# Revit family: 47388 - Ifö Sense High Cabinet with doors, white
name_source: partatom
category: Generic Models
revit_build: Autodesk Revit 2015 (Build: 20140606_1530(x64)
units: mm (PartAtom-declared; Revit-internal decimal feet)

## types (1)
- 47388 - Ifö Sense High Cabinet with doors, white
    BIMObjectName = 47388 - Ifö Sense High Cabinet with doors, white
    Brand = Ifö
    CabinetMaterial = MDF Chipboard
    Category = WashHandBasin
    Color = White
    Depth = 210 mm  [stored 0.688976 ft]
    Description = Ifö Sense half high cabinet with door
    DrainSize = 0 mm  [stored 0 ft]
    Features = feature1, feature2, feature59
    Handle = Metal-Steel
    Height = 1105 mm  [stored 3.62533 ft]
    Manufacturer = Geberit
    Material = MDF Chipboard
    Model = Ifö Sense High Cabinet with doors, white
    ModelNumber = 47388
    ModelReference = Sense
    MountingHeight(offset) = 1365 mm  [stored 4.47835 ft]
    Name = Ifö Sense half high cabinet with door
    NominalDepth = 210 mm  [stored 0.688976 ft]
    NominalHeight = 1105 mm  [stored 3.62533 ft]
    NominalWidth = 320 mm  [stored 1.04987 ft]
    Panel = White
    Serie = Sense
    Shape = Square
    Size = 320x1105x210
    Type = Building element
    URL.dk = http://www.ifo.dk
    URL.no = http://www.ifosanitar.no
    URL.se = http://www.ifo.se
    Width = 320 mm  [stored 1.04987 ft]

note: [stored X ft] marks values corroborated as IEEE doubles in the binary element streams (Revit-internal decimal feet)

## geometry (parser evidence)
native form markers: Sweep x2
no freeform markers — native parametric forms only
